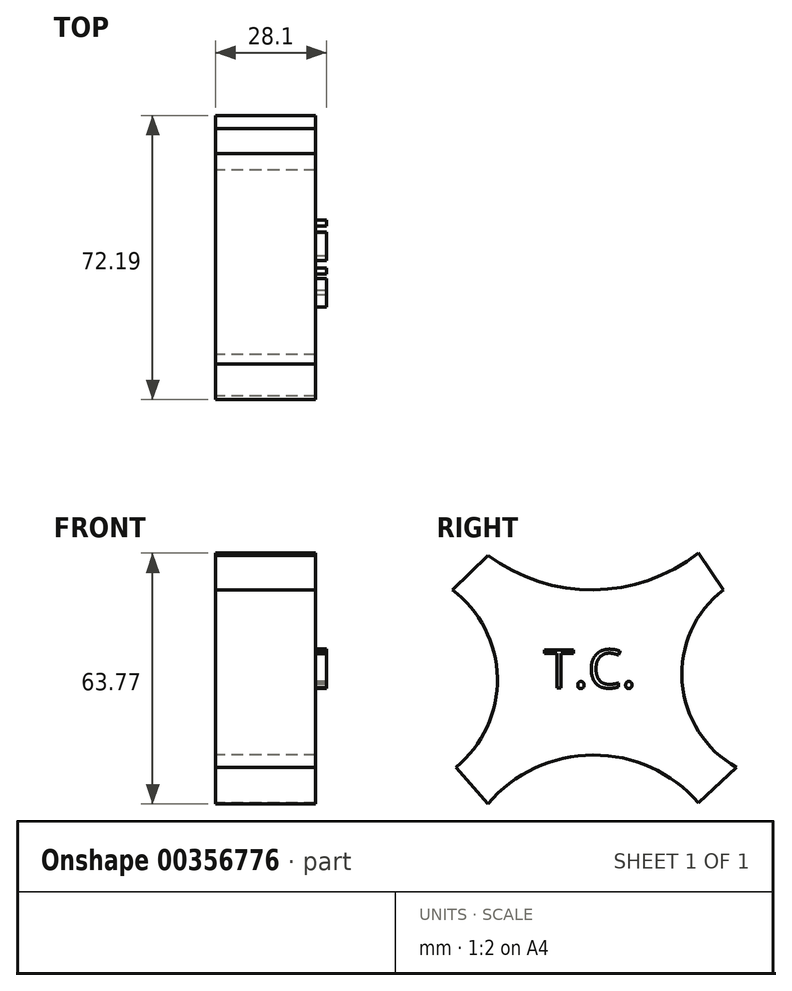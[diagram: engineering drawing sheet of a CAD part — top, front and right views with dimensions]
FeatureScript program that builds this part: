
annotation { "Feature Type Name" : "Feature", "Feature Type Description" : "" }
export const myFeature = defineFeature(function(context is Context, id is Id, definition is map)
    precondition{}
    {
        {
            var Q0;
            Q0=qCreatedBy(makeId("Front.planeOp"),FACE);
            var sketch = newSketch(context, id + "F0", { "sketchPlane" : qUnion([Q0])});
            skCircle(sketch, "E0", {"center": v(-40.9, 37.6) * mm, "radius": 31.68 * mm});
            skCircle(sketch, "E1", {"center": v(37.9, 37.6) * mm, "radius": 31.7 * mm});
            skCircle(sketch, "E2", {"center": v(37.9, -36.7) * mm, "radius": 31.7 * mm});
            skCircle(sketch, "E3", {"center": v(-40.9, -36.7) * mm, "radius": 31.65 * mm});
            skCircle(sketch, "E4", {"center": v(-40.9, 37.6) * mm, "radius": 20.38 * mm});
            skCircle(sketch, "E5", {"center": v(37.9, 37.6) * mm, "radius": 20.42 * mm});
            skCircle(sketch, "E6", {"center": v(37.9, -36.7) * mm, "radius": 20.44 * mm});
            skCircle(sketch, "E7", {"center": v(-40.9, -36.7) * mm, "radius": 20.07 * mm});
            skSolve(sketch);
        }
        {
            var Q0;
            Q0=qSketchRegion(id+"F0",true);
            extrude(context, id + "F1", {"entities" : qUnion([Q0]), "depth" : 25.4 * mm});
        }
        {
            var Q0;
            Q0=qCreatedBy(makeId("Right.planeOp"),FACE);
            var sketch = newSketch(context, id + "F2", { "sketchPlane" : qUnion([Q0])});
            skArc(sketch, "E8", {"start": v(11.13, 30.68) * mm, "mid": v(38, 21.95) * mm, "end": v(64.67, 31.28) * mm});
            skArc(sketch, "E9", {"start": v(3, -23.16) * mm, "mid": v(13.55, -0.39) * mm, "end": v(2.1, 21.95) * mm});
            skPoint(sketch, "E9.endSnap0", {"position": v(38, 21.95) * mm});
            skArc(sketch, "E10", {"start": v(64.67, -32.18) * mm, "mid": v(37.83, -20.04) * mm, "end": v(11.13, -32.49) * mm});
            skArc(sketch, "E11", {"start": v(70.99, 21.95) * mm, "mid": v(60.5, -1.5) * mm, "end": v(74.3, -23.16) * mm});
            skLineSegment(sketch, "E12", {"start": v(2.1, 21.95) * mm, "end": v(11.13, 30.68) * mm});
            skLineSegment(sketch, "E13", {"start": v(3, -23.16) * mm, "end": v(11.13, -32.49) * mm});
            skLineSegment(sketch, "E14", {"start": v(64.67, -32.18) * mm, "end": v(74.3, -23.16) * mm});
            skLineSegment(sketch, "E15", {"start": v(70.99, 21.95) * mm, "end": v(64.67, 31.28) * mm});
            skSolve(sketch);
        }
        {
            var Q0;
            Q0=qSketchRegion(id+"F2",true);
            extrude(context, id + "F3", {"entities" : qUnion([Q0]), "depth" : 25.4 * mm});
        }
        {
            var Q0;
            Q0=makeQuery(id+"F1.opExtrude","CAP_FACE",FACE,{"disambiguationData":[OSD([sQuery(id+"F0.wireOp",EDGE,"E0"),sQuery(id+"F0.wireOp",EDGE,"E4")])],"isStart":false});
            var Q1;
            Q1=makeQuery(id+"F1.opExtrude","CAP_FACE",FACE,{"disambiguationData":[OSD([sQuery(id+"F0.wireOp",EDGE,"E1"),sQuery(id+"F0.wireOp",EDGE,"E5")])],"isStart":false});
            var Q2;
            Q2=makeQuery(id+"F1.opExtrude","CAP_FACE",FACE,{"disambiguationData":[OSD([sQuery(id+"F0.wireOp",EDGE,"E3"),sQuery(id+"F0.wireOp",EDGE,"E7")])],"isStart":false});
            var Q3;
            Q3=makeQuery(id+"F1.opExtrude","CAP_FACE",FACE,{"disambiguationData":[OSD([sQuery(id+"F0.wireOp",EDGE,"E2"),sQuery(id+"F0.wireOp",EDGE,"E6")])],"isStart":false});
            shell(context, id + "F4", {"entities" : qUnion([Q0, Q1, Q2, Q3]), "thickness" : 2.5 * mm});
        }
        {
            var Q0;
            Q0=makeQuery(id+"F1.opExtrude","SWEPT_BODY",BODY,{"disambiguationData":[OSD([sQuery(id+"F0.wireOp",EDGE,"E0"),sQuery(id+"F0.wireOp",EDGE,"E4")])]});
            deleteBodies(context, id + "F5", {"entities" : qUnion([Q0])});
        }
        {
            var Q0;
            Q0=makeQuery(id+"F1.opExtrude","SWEPT_BODY",BODY,{"disambiguationData":[OSD([sQuery(id+"F0.wireOp",EDGE,"E1"),sQuery(id+"F0.wireOp",EDGE,"E5")])]});
            deleteBodies(context, id + "F6", {"entities" : qUnion([Q0])});
        }
        {
            var Q0;
            Q0=makeQuery(id+"F1.opExtrude","SWEPT_BODY",BODY,{"disambiguationData":[OSD([sQuery(id+"F0.wireOp",EDGE,"E2"),sQuery(id+"F0.wireOp",EDGE,"E6")])]});
            deleteBodies(context, id + "F7", {"entities" : qUnion([Q0])});
        }
        {
            var Q0;
            Q0=makeQuery(id+"F1.opExtrude","SWEPT_BODY",BODY,{"disambiguationData":[OSD([sQuery(id+"F0.wireOp",EDGE,"E3"),sQuery(id+"F0.wireOp",EDGE,"E7")])]});
            deleteBodies(context, id + "F8", {"entities" : qUnion([Q0])});
        }
        {
            var Q0;
            Q0=qCreatedBy(makeId("Right.planeOp"),FACE);
            var sketch = newSketch(context, id + "F9", { "sketchPlane" : qUnion([Q0])});
            skText(sketch, "E16", { "text": "T.C.", "fontName": "OpenSans-Regular.ttf"});
            const initialGuessF9  = {"E16": [0.02546, -0.00296, 1, 0, 0.00977]};
            skSetInitialGuess(sketch, initialGuessF9);
            skSolve(sketch);
        }
        {
            var Q0;
            Q0 = qSketchRegion(id + "F9", true);
            extrude(context, id + "F10", {"entities" : qUnion([Q0]), "operationType" : NewBodyOperationType.ADD, "depth" : 28.1 * mm});
        }
    });
